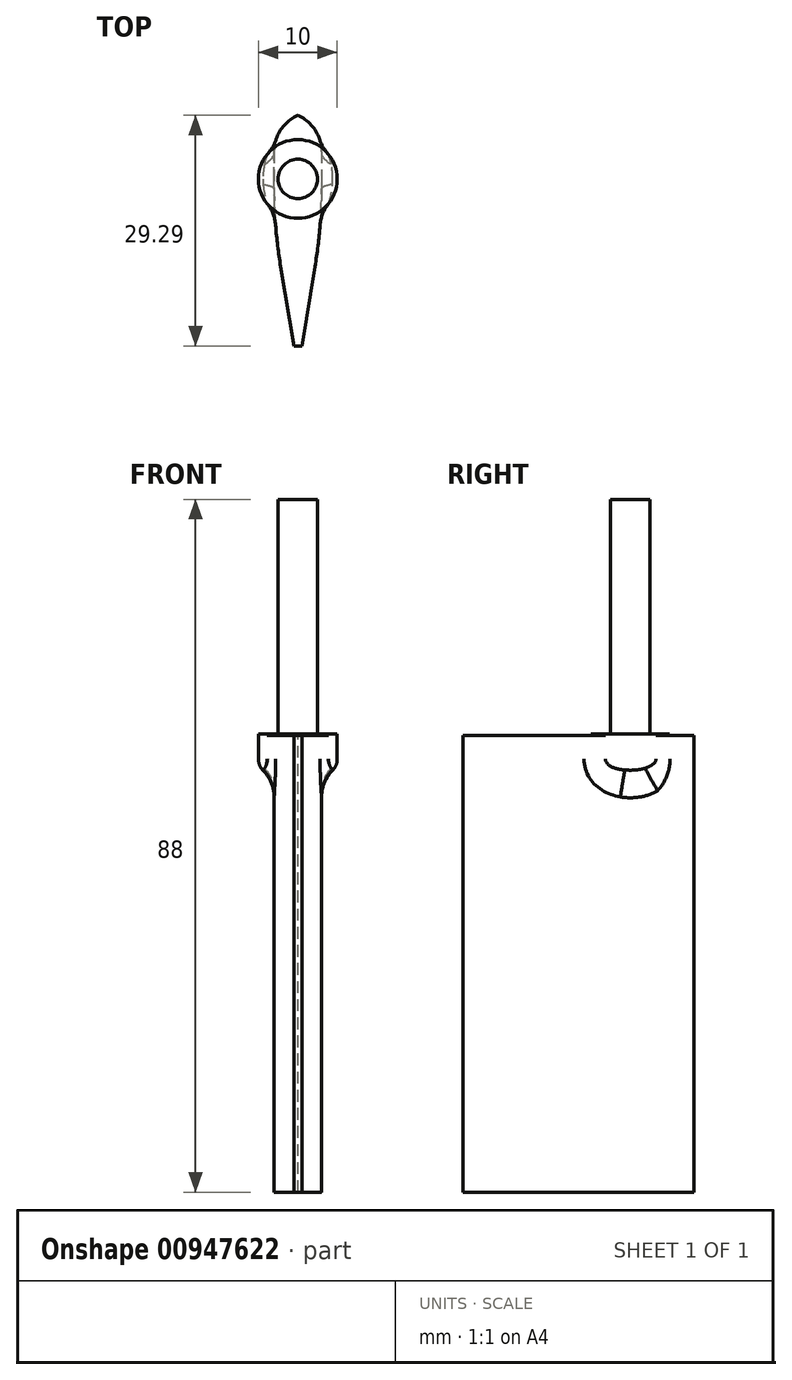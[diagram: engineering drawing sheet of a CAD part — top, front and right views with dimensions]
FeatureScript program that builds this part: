
annotation { "Feature Type Name" : "Feature", "Feature Type Description" : "" }
export const myFeature = defineFeature(function(context is Context, id is Id, definition is map)
    precondition{}
    {
        {
            var Q0;
            Q0=qCreatedBy(makeId("Top.planeOp"),FACE);
            var sketch = newSketch(context, id + "F0", { "sketchPlane" : qUnion([Q0])});
            skCircle(sketch, "E0", {"center": v(0, 0) * mm, "radius": 2.5 * mm});
            skCircle(sketch, "E1", {"center": v(0, 0) * mm, "radius": 5 * mm});
            skLineSegment(sketch, "E2.bottom", {"start": v(-3, 8.5) * mm, "end": v(3, 8.5) * mm});
            skLineSegment(sketch, "E2.top", {"start": v(-3, -21.21) * mm, "end": v(3, -21.21) * mm});
            skLineSegment(sketch, "E2.left", {"start": v(-3, 8.5) * mm, "end": v(-3, -21.21) * mm});
            skLineSegment(sketch, "E2.right", {"start": v(3, 8.5) * mm, "end": v(3, -21.21) * mm});
            skSolve(sketch);
        }
        {
            var Q0;
            Q0=makeQuery(id+"F0.imprint","IMPRINT",FACE,{"disambiguationData":[TD([[makeQuery(id+"F0.imprint","IMPRINT",EDGE,{"derivedFrom":sQuery(id+"F0.wireOp",EDGE,"E0")}),1.0]])]});
            extrude(context, id + "F1", {"entities" : qUnion([Q0]), "depth" : 30 * mm, "offsetDistance" : 25 * mm});
        }
        {
            var Q0;
            {var subQ5=sQuery(id+"F0.wireOp",EDGE,"E2.bottom");Q0=makeQuery(id+"F0.imprint","IMPRINT",FACE,{"disambiguationData":[TD([[makeQuery(id+"F0.imprint","IMPRINT",EDGE,{"derivedFrom":subQ5}),-1.0]])]});}
            var Q1;
            Q1=makeQuery(id+"F0.imprint","IMPRINT",FACE,{"disambiguationData":[TD([[makeQuery(id+"F0.imprint","IMPRINT",EDGE,{"derivedFrom":sQuery(id+"F0.wireOp",EDGE,"E0")}),-1.0]])]});
            var Q2;
            {var subQ5=sQuery(id+"F0.wireOp",EDGE,"E2.top");Q2=makeQuery(id+"F0.imprint","IMPRINT",FACE,{"disambiguationData":[TD([[makeQuery(id+"F0.imprint","IMPRINT",EDGE,{"derivedFrom":subQ5}),1.0]])]});}
            var Q3;
            Q3=makeQuery(id+"F0.imprint","IMPRINT",FACE,{"disambiguationData":[TD([[makeQuery(id+"F0.imprint","IMPRINT",EDGE,{"derivedFrom":sQuery(id+"F0.wireOp",EDGE,"E0")}),1.0]])]});
            extrude(context, id + "F2", {"entities" : qUnion([Q0, Q1, Q2, Q3]), "operationType" : NewBodyOperationType.ADD, "oppositeDirection" : true, "depth" : 58 * mm, "offsetDistance" : 25 * mm});
        }
        {
            var Q0;
            {var subQ0=sQuery(id+"F0.wireOp",EDGE,"E2.left");var subQ1=sQuery(id+"F0.wireOp",EDGE,"E1");var subQ2=makeQuery(id+"F0.imprint","INTERSECT",VERTEX,{"disambiguationData":[OD(0.0)],"derivedFrom":[subQ1,subQ0]});Q0=makeQuery(id+"F0.imprint","IMPRINT",FACE,{"disambiguationData":[TD([[makeQuery(id+"F0.imprint","IMPRINT",EDGE,{"disambiguationData":[TD([[subQ2,-1.0]])],"derivedFrom":subQ1}),1.0]])]});}
            var Q1;
            {var subQ0=sQuery(id+"F0.wireOp",EDGE,"E2.right");var subQ1=sQuery(id+"F0.wireOp",EDGE,"E1");var subQ2=makeQuery(id+"F0.imprint","INTERSECT",VERTEX,{"disambiguationData":[OD(0.0)],"derivedFrom":[subQ1,subQ0]});Q1=makeQuery(id+"F0.imprint","IMPRINT",FACE,{"disambiguationData":[TD([[makeQuery(id+"F0.imprint","IMPRINT",EDGE,{"disambiguationData":[TD([[subQ2,1.0]])],"derivedFrom":subQ1}),1.0]])]});}
            extrude(context, id + "F3", {"entities" : qUnion([Q0, Q1]), "operationType" : NewBodyOperationType.ADD, "oppositeDirection" : true, "depth" : 5 * mm, "offsetDistance" : 25 * mm});
        }
        {
            var Q0;
            Q0=makeQuery(id+"F2.opExtrude","SWEPT_EDGE",EDGE,{"disambiguationData":[OSD([sQuery(id+"F0.wireOp",EDGE,"E2.bottom"),sQuery(id+"F0.wireOp",EDGE,"E2.right")])]});
            var Q1;
            Q1=makeQuery(id+"F2.opExtrude","SWEPT_EDGE",EDGE,{"disambiguationData":[OSD([sQuery(id+"F0.wireOp",EDGE,"E2.bottom"),sQuery(id+"F0.wireOp",EDGE,"E2.left")])]});
            fillet(context, id + "F4", {"entities" : qUnion([Q0, Q1]), "radius" : 5 * mm, "tangentPropagation" : true, "allowEdgeOverflow" : false});
        }
        {
            var Q0;
            Q0=makeQuery(id+"F2.opExtrude","SWEPT_EDGE",EDGE,{"disambiguationData":[OSD([sQuery(id+"F0.wireOp",EDGE,"E2.top"),sQuery(id+"F0.wireOp",EDGE,"E2.right")])]});
            var Q1;
            Q1=makeQuery(id+"F2.opExtrude","SWEPT_EDGE",EDGE,{"disambiguationData":[OSD([sQuery(id+"F0.wireOp",EDGE,"E2.top"),sQuery(id+"F0.wireOp",EDGE,"E2.left")])]});
            chamfer(context, id + "F5", {"entities" : qUnion([Q0, Q1]), "chamferType" : ChamferType.TWO_OFFSETS, "width1" : 2.5 * mm, "oppositeDirection" : false, "width2" : 15 * mm, "tangentPropagation" : true});
        }
        {
            var Q0;
            {var subQ0=sQuery(id+"F0.wireOp",EDGE,"E2.right");Q0=makeQuery(id+"F5.opChamfer","BLEND_EDGE",EDGE,{"blendedFrom":[makeQuery(id+"F2.opExtrude","SWEPT_EDGE",EDGE,{"disambiguationData":[OSD([sQuery(id+"F0.wireOp",EDGE,"E2.top"),subQ0])]}),makeQuery(id+"F2.opExtrude","SWEPT_FACE",FACE,{"disambiguationData":[OSD([subQ0])]})],"blendedInto":[makeQuery(id+"F2.opExtrude","SWEPT_FACE",FACE,{"disambiguationData":[OSD([subQ0])]})]});}
            var Q1;
            {var subQ0=sQuery(id+"F0.wireOp",EDGE,"E2.left");Q1=makeQuery(id+"F5.opChamfer","BLEND_EDGE",EDGE,{"blendedFrom":[makeQuery(id+"F2.opExtrude","SWEPT_EDGE",EDGE,{"disambiguationData":[OSD([sQuery(id+"F0.wireOp",EDGE,"E2.top"),subQ0])]}),makeQuery(id+"F2.opExtrude","SWEPT_FACE",FACE,{"disambiguationData":[OSD([subQ0])]})],"blendedInto":[makeQuery(id+"F2.opExtrude","SWEPT_FACE",FACE,{"disambiguationData":[OSD([subQ0])]})]});}
            fillet(context, id + "F6", {"entities" : qUnion([Q0, Q1]), "radius" : 60 * mm, "tangentPropagation" : true, "allowEdgeOverflow" : false});
        }
        {
            var Q0;
            {var subQ0=sQuery(id+"F0.wireOp",EDGE,"E2.right");var subQ1=sQuery(id+"F0.wireOp",EDGE,"E1");Q0=makeQuery(id+"F3.opExtrude","CAP_EDGE",EDGE,{"disambiguationData":[OSD([subQ1]),TDD([makeQuery(id+"F0.imprint","IMPRINT",EDGE,{"disambiguationData":[TD([[makeQuery(id+"F0.imprint","INTERSECT",VERTEX,{"disambiguationData":[OD(0.0)],"derivedFrom":[subQ1,subQ0]}),1.0]])],"derivedFrom":subQ1})])],"isStart":false});}
            var Q1;
            {var subQ0=sQuery(id+"F0.wireOp",EDGE,"E2.left");var subQ1=sQuery(id+"F0.wireOp",EDGE,"E1");Q1=makeQuery(id+"F3.opExtrude","CAP_EDGE",EDGE,{"disambiguationData":[OSD([subQ1]),TDD([makeQuery(id+"F0.imprint","IMPRINT",EDGE,{"disambiguationData":[TD([[makeQuery(id+"F0.imprint","INTERSECT",VERTEX,{"disambiguationData":[OD(0.0)],"derivedFrom":[subQ1,subQ0]}),-1.0]])],"derivedFrom":subQ1})])],"isStart":false});}
            fillet(context, id + "F7", {"entities" : qUnion([Q0, Q1]), "radius" : 2 * mm, "tangentPropagation" : true, "allowEdgeOverflow" : false});
        }
        {
            var Q0;
            {var subQ0=sQuery(id+"F0.wireOp",EDGE,"E2.left");var subQ1=sQuery(id+"F0.wireOp",EDGE,"E1");Q0=makeQuery(id+"F4.opFillet","BLEND_EDGE",EDGE,{"blendedFrom":[makeQuery(id+"F2.opExtrude","SWEPT_EDGE",EDGE,{"disambiguationData":[OSD([sQuery(id+"F0.wireOp",EDGE,"E2.bottom"),subQ0])]}),makeQuery(id+"F3.opExtrude","SWEPT_FACE",FACE,{"disambiguationData":[OSD([subQ1]),TDD([makeQuery(id+"F0.imprint","IMPRINT",EDGE,{"disambiguationData":[TD([[makeQuery(id+"F0.imprint","INTERSECT",VERTEX,{"disambiguationData":[OD(0.0)],"derivedFrom":[subQ1,subQ0]}),-1.0]])],"derivedFrom":subQ1})])]})],"blendedInto":[makeQuery(id+"F3.opExtrude","SWEPT_FACE",FACE,{"disambiguationData":[OSD([subQ1]),TDD([makeQuery(id+"F0.imprint","IMPRINT",EDGE,{"disambiguationData":[TD([[makeQuery(id+"F0.imprint","INTERSECT",VERTEX,{"disambiguationData":[OD(0.0)],"derivedFrom":[subQ1,subQ0]}),-1.0]])],"derivedFrom":subQ1})])]})]});}
            var Q1;
            {var subQ0=sQuery(id+"F0.wireOp",EDGE,"E2.right");var subQ1=sQuery(id+"F0.wireOp",EDGE,"E1");Q1=makeQuery(id+"F6.opFillet","BLEND_EDGE",EDGE,{"blendedFrom":[makeQuery(id+"F5.opChamfer","BLEND_EDGE",EDGE,{"blendedFrom":[makeQuery(id+"F2.opExtrude","SWEPT_EDGE",EDGE,{"disambiguationData":[OSD([sQuery(id+"F0.wireOp",EDGE,"E2.top"),subQ0])]}),makeQuery(id+"F2.opExtrude","SWEPT_FACE",FACE,{"disambiguationData":[OSD([subQ0])]})],"blendedInto":[makeQuery(id+"F2.opExtrude","SWEPT_FACE",FACE,{"disambiguationData":[OSD([subQ0])]})]}),makeQuery(id+"F3.opExtrude","SWEPT_FACE",FACE,{"disambiguationData":[OSD([subQ1]),TDD([makeQuery(id+"F0.imprint","IMPRINT",EDGE,{"disambiguationData":[TD([[makeQuery(id+"F0.imprint","INTERSECT",VERTEX,{"disambiguationData":[OD(0.0)],"derivedFrom":[subQ1,subQ0]}),1.0]])],"derivedFrom":subQ1})])]})],"blendedInto":[makeQuery(id+"F3.opExtrude","SWEPT_FACE",FACE,{"disambiguationData":[OSD([subQ1]),TDD([makeQuery(id+"F0.imprint","IMPRINT",EDGE,{"disambiguationData":[TD([[makeQuery(id+"F0.imprint","INTERSECT",VERTEX,{"disambiguationData":[OD(0.0)],"derivedFrom":[subQ1,subQ0]}),1.0]])],"derivedFrom":subQ1})])]})]});}
            fillet(context, id + "F8", {"entities" : qUnion([Q0, Q1]), "radius" : 5 * mm, "tangentPropagation" : true, "allowEdgeOverflow" : false});
        }
        {
            var Q0;
            {var subQ0=sQuery(id+"F0.wireOp",EDGE,"E2.right");var subQ1=sQuery(id+"F0.wireOp",EDGE,"E1");var subQ2=makeQuery(id+"F0.imprint","INTERSECT",VERTEX,{"disambiguationData":[OD(0.0)],"derivedFrom":[subQ1,subQ0]});Q0=makeQuery(id+"F0.imprint","IMPRINT",FACE,{"disambiguationData":[TD([[makeQuery(id+"F0.imprint","IMPRINT",EDGE,{"disambiguationData":[TD([[subQ2,1.0]])],"derivedFrom":subQ1}),1.0]])]});}
            var Q1;
            Q1=makeQuery(id+"F0.imprint","IMPRINT",FACE,{"disambiguationData":[TD([[makeQuery(id+"F0.imprint","IMPRINT",EDGE,{"derivedFrom":sQuery(id+"F0.wireOp",EDGE,"E0")}),-1.0]])]});
            var Q2;
            {var subQ0=sQuery(id+"F0.wireOp",EDGE,"E2.left");var subQ1=sQuery(id+"F0.wireOp",EDGE,"E1");var subQ2=makeQuery(id+"F0.imprint","INTERSECT",VERTEX,{"disambiguationData":[OD(0.0)],"derivedFrom":[subQ1,subQ0]});Q2=makeQuery(id+"F0.imprint","IMPRINT",FACE,{"disambiguationData":[TD([[makeQuery(id+"F0.imprint","IMPRINT",EDGE,{"disambiguationData":[TD([[subQ2,-1.0]])],"derivedFrom":subQ1}),1.0]])]});}
            extrude(context, id + "F9", {"entities" : qUnion([Q0, Q1, Q2]), "operationType" : NewBodyOperationType.ADD, "depth" : 0.2 * mm, "offsetDistance" : 25 * mm});
        }
    });
